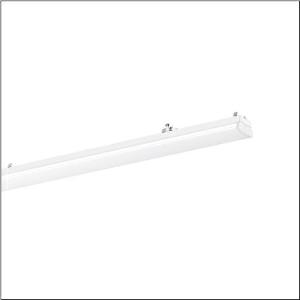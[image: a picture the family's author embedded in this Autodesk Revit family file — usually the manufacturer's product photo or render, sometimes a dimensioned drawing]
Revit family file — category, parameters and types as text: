
# Revit family: licross_r__21_recessed_opal_mo_52tl1ddn425g_d02a
name_source: partatom
category: Lighting Fixtures
units: mm (PartAtom-declared; Revit-internal decimal feet)

## family parameters
Cut with Voids When Loaded = No
Host = Face
Light Source = No
Part Type = Normal
Room Calculation Point = No
Round Connector Dimension = Use Diameter
Shared = No

## types (1)
- --- (1 x LED, 2750 lm, 16.2 W, 4000K)
    Apparent Load = 16 VA
    CIE Flux Codes = 44 73 91 87 100
    Color Rendering = 80
    Color Temperature = 4000K
    Default Elevation = 1800 mm
    Description = Licross® 21 recessed opal MO, luminaire insert, of sheet steel, galvanised, coil coated, white, length: 1.500mm, width: 66mm, height: 67mm, LED rated luminous flux: 2.750lm, light colour: 840, control gear: DALI 2, with plug, 5-pole, with phase selection, mains connection: 220..240V, AC, 50/60Hz, rated input power: 16W, halogen-free wiring, primary optical cover: cover, of PMMA, light emission: direct with ceiling illumination distribution, primary light characteristic: symmetric, protection rating (complete): IP40, insulation class (complete): insulation class I (protective earthing), certification: CE, ENEC, VDE, UKCA, protection symbol: D if used in an environment without relevant dust loads with corresponding accessories, impact resistance: IK06, permissible ambient temperature for indoor applications: -25..+50°C, corresponds to IFS (International Featured Standards) requirements for safety and quality in the food industry, reducing of maximum allowable ambient temperature of 5°C with ceiling mounting, LABS conformity tested according to VDMA 24364:2018-05, packaging unit: 1 piece
    Height = 83 mm
    Lamp = 1 x LED
    Lamp Light Flux = 2750 lm
    Lamp Power = 16.2 W
    Lamp count = 1
    Length = 1500 mm
    Luminous efficacy = 170 lm/W
    Manufacturer = Siteco
    ModVariant = No
    Model = 52TL1DDN425G
    Mounting Place = Ceiling
    Mounting Type = Pendant
    Number of Poles = 1
    OnlyDefault = Yes
    Power Factor = 1
    Product Name = Licross® 21 recessed opal MO
    Product group = luminaire insert
    ProductGroupID = 901
    Protection Class = Protection class I
    Protection Degree = IP 40
    RLX_Detail_Level = 1
    RLX_Emergency_Light_Flux = 0 lm
    RLX_Emergency_Type = 0
    RLX_Emergency_Type_DB = No
    RlxData = <blob elided: 26225 chars, md5=233a9e89>
    Socket = socket
    Standby Power = 0 W
    System Light Flux = 2750 lm
    System Power = 16 W
    Type Comments = factory setting: luminous flux: 100 % | dim-lin: 254 | 104 mA
    Type Image = l_1313666.jpg
    URL = http://relux.com
    VarID = @adj_022405
    Voltage = 0 V
    Weight = 0.00 kg
    Width = 76 mm

## geometry (parser evidence)
native form markers: Blend x4, Sweep x14
no freeform markers — native parametric forms only
